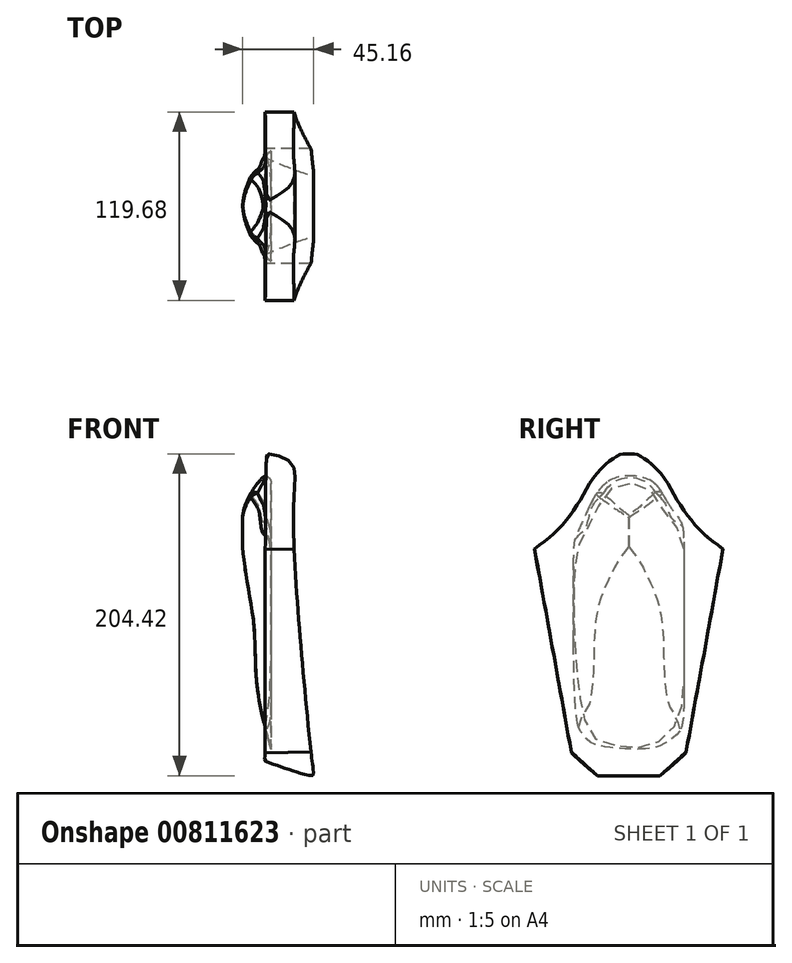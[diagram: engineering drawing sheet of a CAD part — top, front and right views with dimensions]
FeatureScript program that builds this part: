
annotation { "Feature Type Name" : "Feature", "Feature Type Description" : "" }
export const myFeature = defineFeature(function(context is Context, id is Id, definition is map)
    precondition{}
    {
        {
            var Q0;
            Q0=qCreatedBy(makeId("Right.planeOp"),FACE);
            var sketch = newSketch(context, id + "F0", { "sketchPlane" : qUnion([Q0])});
            skFitSpline(sketch, "E0", {"points": [v(0, 116.17) * mm, v(3.06, 115.78) * mm, v(7.67, 113.9) * mm, v(14.22, 108.94) * mm, v(22.25, 100.28) * mm, v(32.3, 83.46) * mm, v(42.34, 70.02) * mm, v(50.07, 62.3) * mm, v(59.84, 54.97) * mm], "startDerivative": vector(42.97, -3.15) * mm, "endDerivative": vector(75.08, -53.22) * mm});
            skLineSegment(sketch, "E1", {"start": v(59.84, 54.97) * mm, "end": v(36.42, -74.25) * mm});
            skLineSegment(sketch, "E2", {"start": v(36.42, -74.25) * mm, "end": v(17.78, -91.38) * mm});
            skLineSegment(sketch, "E3", {"start": v(17.78, -91.38) * mm, "end": v(0, -91.38) * mm});
            skLineSegment(sketch, "E4.MirrorCS", {"start": v(-59.84, 54.97) * mm, "end": v(-36.42, -74.25) * mm});
            skLineSegment(sketch, "E5.MirrorCS", {"start": v(-36.42, -74.25) * mm, "end": v(-17.78, -91.38) * mm});
            skLineSegment(sketch, "E6.MirrorCS", {"start": v(-17.78, -91.38) * mm, "end": v(0, -91.38) * mm});
            skFitSpline(sketch, "E7.MirrorCS", {"points": [v(0, 116.17) * mm, v(-3.06, 115.78) * mm, v(-7.67, 113.9) * mm, v(-14.22, 108.94) * mm, v(-22.25, 100.28) * mm, v(-32.3, 83.46) * mm, v(-42.34, 70.02) * mm, v(-50.07, 62.3) * mm, v(-59.84, 54.97) * mm], "startDerivative": vector(-42.97, -3.15) * mm, "endDerivative": vector(-75.08, -53.22) * mm});
            skSolve(sketch);
        }
        {
            var Q0;
            Q0=makeQuery(id+"F0.imprint","IMPRINT",FACE,{"disambiguationData":[TD([[makeQuery(id+"F0.imprint","IMPRINT",EDGE,{"derivedFrom":sQuery(id+"F0.wireOp",EDGE,"E0")}),-1.0]])]});
            extrude(context, id + "F1", {"entities" : qUnion([Q0]), "depth" : 100 * mm, "offsetDistance" : 25 * mm});
        }
        {
            var Q0;
            Q0=qCreatedBy(makeId("Front.planeOp"),FACE);
            cPlane(context, id + "F2", {"entities" : qUnion([Q0]), "cplaneType" : CPlaneType.OFFSET, "offset" : 75 * mm, "width" : 150 * mm, "height" : 150 * mm});
        }
        {
            var Q0;
            Q0=qCreatedBy(id+"F2.planeOp",FACE);
            var sketch = newSketch(context, id + "F3", { "sketchPlane" : qUnion([Q0])});
            skFitSpline(sketch, "E8", {"points": [v(31.56, 115.61) * mm, v(44.65, 110.3) * mm, v(46.26, 81.32) * mm, v(54.88, -85.85) * mm, v(53.7, -89.38) * mm, v(25.68, -79.97) * mm, v(24.31, -77.23) * mm, v(29.8, 112.28) * mm, v(31.56, 115.61) * mm]});
            skSolve(sketch);
        }
        {
            var Q0;
            Q0=makeQuery(id+"F3.imprint","IMPRINT",FACE,{"disambiguationData":[TD([[makeQuery(id+"F3.imprint","IMPRINT",EDGE,{"derivedFrom":sQuery(id+"F3.wireOp",EDGE,"E8")}),-1.0]])]});
            extrude(context, id + "F4", {"entities" : qUnion([Q0]), "oppositeDirection" : true, "depth" : 146 * mm, "offsetDistance" : 25 * mm});
        }
        {
            var Q0;
            Q0=makeQuery(id+"F1.opExtrude","SWEPT_BODY",BODY,{"disambiguationData":[OSD([sQuery(id+"F0.wireOp",EDGE,"E0"),sQuery(id+"F0.wireOp",EDGE,"E1"),sQuery(id+"F0.wireOp",EDGE,"E2"),sQuery(id+"F0.wireOp",EDGE,"E3"),sQuery(id+"F0.wireOp",EDGE,"E4.MirrorCS"),sQuery(id+"F0.wireOp",EDGE,"E5.MirrorCS"),sQuery(id+"F0.wireOp",EDGE,"E6.MirrorCS"),sQuery(id+"F0.wireOp",EDGE,"E7.MirrorCS")])]});
            var Q1;
            Q1=makeQuery(id+"F4.opExtrude","SWEPT_BODY",BODY,{"disambiguationData":[OSD([sQuery(id+"F3.wireOp",EDGE,"E8")])]});
            booleanBodies(context, id + "F5", {"operationType" : BooleanOperationType.INTERSECTION, "tools" : qUnion([Q0, Q1])});
        }
        {
            var Q0;
            Q0=qCreatedBy(makeId("Top.planeOp"),FACE);
            cPlane(context, id + "F6", {"entities" : qUnion([Q0]), "cplaneType" : CPlaneType.OFFSET, "offset" : 90 * mm, "oppositeDirection" : true, "width" : 150 * mm, "height" : 150 * mm});
        }
        {
            var Q0;
            Q0=qCreatedBy(id+"F6.planeOp",FACE);
            var sketch = newSketch(context, id + "F7", { "sketchPlane" : qUnion([Q0])});
            skLineSegment(sketch, "E9", {"start": v(24.4, -31.72) * mm, "end": v(24.4, 31.99) * mm});
            skFitSpline(sketch, "E10", {"points": [v(24.4, -31.72) * mm, v(24, -30.15) * mm, v(23.4, -28.17) * mm, v(22.63, -25.84) * mm, v(21.8, -23.1) * mm, v(20.57, -19.74) * mm, v(19.28, -18.14) * mm, v(17.6, -15.89) * mm, v(16, -11.54) * mm, v(15.35, -7.88) * mm, v(15.2, -4.37) * mm, v(15.16, -0.02) * mm], "startDerivative": vector(-5.56, 22.83) * mm, "endDerivative": vector(-0.25, 40.72) * mm});
            skFitSpline(sketch, "E11.MirrorCS", {"points": [v(24.4, 31.72) * mm, v(24, 30.15) * mm, v(23.4, 28.17) * mm, v(22.63, 25.84) * mm, v(21.8, 23.1) * mm, v(20.57, 19.74) * mm, v(19.28, 18.14) * mm, v(17.6, 15.89) * mm, v(16, 11.54) * mm, v(15.35, 7.88) * mm, v(15.2, 4.37) * mm, v(15.16, 0.02) * mm], "startDerivative": vector(-5.56, -22.83) * mm, "endDerivative": vector(-0.25, -40.72) * mm});
            skFitSpline(sketch, "E12", {"points": [v(15.16, -0.02) * mm, v(15.16, 0.02) * mm], "startDerivative": vector(0, 0.04) * mm, "endDerivative": vector(0, 0.04) * mm});
            skSolve(sketch);
        }
        {
            var Q0;
            Q0=makeQuery(id+"F5.opBoolean","INTERSECT",BODY,{"derivedFrom":[makeQuery(id+"F1.opExtrude","SWEPT_BODY",BODY,{"disambiguationData":[OSD([sQuery(id+"F0.wireOp",EDGE,"E0"),sQuery(id+"F0.wireOp",EDGE,"E1"),sQuery(id+"F0.wireOp",EDGE,"E2"),sQuery(id+"F0.wireOp",EDGE,"E3"),sQuery(id+"F0.wireOp",EDGE,"E4.MirrorCS"),sQuery(id+"F0.wireOp",EDGE,"E5.MirrorCS"),sQuery(id+"F0.wireOp",EDGE,"E6.MirrorCS"),sQuery(id+"F0.wireOp",EDGE,"E7.MirrorCS")])]}),makeQuery(id+"F4.opExtrude","SWEPT_BODY",BODY,{"disambiguationData":[OSD([sQuery(id+"F3.wireOp",EDGE,"E8")])]})]});
            transform(context, id + "F8", {"entities" : qUnion([Q0]), "transformType" : TransformType.TRANSLATION_3D, "dx" : -23.7 * mm, "dy" : 0 * mm, "dz" : 0 * mm, "makeCopy" : false});
        }
        {
            var Q0;
            {var subQ0=sQuery(id+"F7.wireOp",EDGE,"E10");Q0=makeQuery(id+"F7.imprint","IMPRINT",FACE,{"disambiguationData":[TD([[makeQuery(id+"F7.imprint","IMPRINT",EDGE,{"derivedFrom":subQ0}),-1.0]])]});}
            extrude(context, id + "F9", {"entities" : qUnion([Q0]), "oppositeDirection" : true, "depth" : 25 * mm, "offsetDistance" : 25 * mm});
        }
        {
            var Q0;
            Q0=makeQuery(id+"F5.opBoolean","INTERSECT",BODY,{"derivedFrom":[makeQuery(id+"F1.opExtrude","SWEPT_BODY",BODY,{"disambiguationData":[OSD([sQuery(id+"F0.wireOp",EDGE,"E0"),sQuery(id+"F0.wireOp",EDGE,"E1"),sQuery(id+"F0.wireOp",EDGE,"E2"),sQuery(id+"F0.wireOp",EDGE,"E3"),sQuery(id+"F0.wireOp",EDGE,"E4.MirrorCS"),sQuery(id+"F0.wireOp",EDGE,"E5.MirrorCS"),sQuery(id+"F0.wireOp",EDGE,"E6.MirrorCS"),sQuery(id+"F0.wireOp",EDGE,"E7.MirrorCS")])]}),makeQuery(id+"F4.opExtrude","SWEPT_BODY",BODY,{"disambiguationData":[OSD([sQuery(id+"F3.wireOp",EDGE,"E8")])]})]});
            var Q1;
            Q1=makeQuery(id+"F9.opExtrude","CAP_EDGE",EDGE,{"disambiguationData":[OSD([sQuery(id+"F7.wireOp",EDGE,"E9")])],"isStart":true});
            transform(context, id + "F10", {"entities" : qUnion([Q0]), "transformType" : TransformType.ROTATION, "transformAxis" : qUnion([Q1]), "angle" : 1.35 * degree, "oppositeDirection" : true, "makeCopy" : false});
        }
        {
            var Q0;
            Q0=makeQuery(id+"F9.opExtrude","SWEPT_BODY",BODY,{"disambiguationData":[OSD([sQuery(id+"F7.wireOp",EDGE,"E9"),sQuery(id+"F7.wireOp",EDGE,"E10"),sQuery(id+"F7.wireOp",EDGE,"E11.MirrorCS"),sQuery(id+"F7.wireOp",EDGE,"E12")])]});
            deleteBodies(context, id + "F11", {"entities" : qUnion([Q0])});
        }
        {
            var Q0;
            Q0=qCreatedBy(makeId("Front.planeOp"),FACE);
            var sketch = newSketch(context, id + "F12", { "sketchPlane" : qUnion([Q0])});
            skLineSegment(sketch, "E13", {"start": v(-30.4, 103.45) * mm, "end": v(-30.4, -72.87) * mm});
            skFitSpline(sketch, "E14", {"points": [v(-30.4, 103.45) * mm, v(-35.45, 100.36) * mm, v(-43.9, 89.17) * mm, v(-48.84, 73.76) * mm, v(-47.56, 46.6) * mm, v(-43.7, 22.57) * mm, v(-40.96, 0.92) * mm, v(-39.3, -33.03) * mm, v(-30.4, -72.87) * mm], "startDerivative": vector(-74.42, -34.6) * mm, "endDerivative": vector(64.25, -232.85) * mm});
            skSolve(sketch);
        }
        {
            var Q0;
            Q0=makeQuery(id+"F12.imprint","IMPRINT",FACE,{"disambiguationData":[TD([[makeQuery(id+"F12.imprint","IMPRINT",EDGE,{"derivedFrom":sQuery(id+"F12.wireOp",EDGE,"E13")}),-1.0]])]});
            extrude(context, id + "F13", {"entities" : qUnion([Q0]), "endBound" : BoundingType.SYMMETRIC, "depth" : 70 * mm, "offsetDistance" : 25 * mm});
        }
        {
            var Q0;
            Q0=qCreatedBy(id+"F6.planeOp",FACE);
            var sketch = newSketch(context, id + "F14", { "sketchPlane" : qUnion([Q0])});
            skFitSpline(sketch, "E15", {"points": [v(-29.59, -35.48) * mm, v(-31.45, -34.37) * mm, v(-35.74, -30.03) * mm, v(-37.5, -25.37) * mm, v(-40.16, -22.47) * mm, v(-43.6, -18.28) * mm, v(-46.11, -12.1) * mm, v(-47.49, -7.52) * mm, v(-48.63, -0.12) * mm], "startDerivative": vector(-19.9, 10.35) * mm, "endDerivative": vector(-6.7, 52.44) * mm});
            skFitSpline(sketch, "E16.MirrorCS", {"points": [v(-29.59, 35.48) * mm, v(-31.45, 34.37) * mm, v(-35.74, 30.03) * mm, v(-37.5, 25.37) * mm, v(-40.16, 22.47) * mm, v(-43.6, 18.28) * mm, v(-46.11, 12.1) * mm, v(-47.49, 7.52) * mm, v(-48.63, 0.12) * mm], "startDerivative": vector(-19.9, -10.35) * mm, "endDerivative": vector(-6.7, -52.44) * mm});
            skFitSpline(sketch, "E17", {"points": [v(-48.63, -0.12) * mm, v(-48.63, 0.12) * mm], "startDerivative": vector(0, 0.24) * mm, "endDerivative": vector(0, 0.24) * mm});
            skFitSpline(sketch, "E18", {"points": [v(-29.59, -35.48) * mm, v(-33.07, -37.37) * mm, v(-41.1, -38.88) * mm, v(-50.76, -37.59) * mm, v(-55.94, -17.68) * mm, v(-56.15, 12.74) * mm, v(-57.23, 36.15) * mm, v(-50.92, 40.3) * mm, v(-41.7, 39.77) * mm, v(-30.96, 36.53) * mm, v(-29.59, 35.48) * mm], "startDerivative": vector(-51.56, -34.67) * mm, "endDerivative": vector(23.33, -25.13) * mm});
            skSolve(sketch);
        }
        {
            var Q0;
            Q0=makeQuery(id+"F14.imprint","IMPRINT",FACE,{"disambiguationData":[TD([[makeQuery(id+"F14.imprint","IMPRINT",EDGE,{"derivedFrom":sQuery(id+"F14.wireOp",EDGE,"E15")}),1.0]])]});
            extrude(context, id + "F15", {"entities" : qUnion([Q0]), "operationType" : NewBodyOperationType.REMOVE, "depth" : 196.6 * mm, "offsetDistance" : 25 * mm});
        }
        {
            var Q0;
            Q0=qCreatedBy(makeId("Right.planeOp"),FACE);
            cPlane(context, id + "F16", {"entities" : qUnion([Q0]), "cplaneType" : CPlaneType.OFFSET, "offset" : 55.8 * mm, "oppositeDirection" : true, "width" : 150 * mm, "height" : 150 * mm});
        }
        {
            var Q0;
            Q0=qCreatedBy(id+"F16.planeOp",FACE);
            var sketch = newSketch(context, id + "F17", { "sketchPlane" : qUnion([Q0])});
            skFitSpline(sketch, "E19", {"points": [v(38.7, 61.75) * mm, v(28.45, 78.99) * mm, v(20.37, 91.64) * mm, v(14.45, 97.92) * mm, v(2.05, 101.46) * mm, v(-11.23, 98.68) * mm, v(-21.52, 88.15) * mm, v(-32.87, 65.68) * mm, v(-38.32, 51.93) * mm, v(-33.3, -53.67) * mm, v(-21.08, -71.78) * mm, v(-7.56, -75.06) * mm, v(5.1, -76.37) * mm, v(21.25, -72.22) * mm, v(35, -57.6) * mm, v(39.57, -36.87) * mm, v(38.7, 61.75) * mm]});
            skCircle(sketch, "E20", {"center": v(2.4, 18.7) * mm, "radius": 126.46 * mm});
            skSolve(sketch);
        }
        {
            var Q0;
            Q0=makeQuery(id+"F17.imprint","IMPRINT",FACE,{"disambiguationData":[TD([[makeQuery(id+"F17.imprint","IMPRINT",EDGE,{"derivedFrom":sQuery(id+"F17.wireOp",EDGE,"E19")}),-1.0]])]});
            extrude(context, id + "F18", {"entities" : qUnion([Q0]), "operationType" : NewBodyOperationType.REMOVE, "depth" : 46 * mm, "offsetDistance" : 25 * mm});
        }
        {
            var Q0;
            Q0=makeQuery(id+"F13.opExtrude","SWEPT_BODY",BODY,{"disambiguationData":[OSD([sQuery(id+"F12.wireOp",EDGE,"E13"),sQuery(id+"F12.wireOp",EDGE,"E14")])]});
            transform(context, id + "F19", {"entities" : qUnion([Q0]), "transformType" : TransformType.TRANSLATION_3D, "dx" : 34.8 * mm, "dy" : 0 * mm, "dz" : 0 * mm, "makeCopy" : false});
        }
        {
            var Q0;
            Q0=makeQuery(id+"F15.boolean.opBoolean","SPLIT",FACE,{"disambiguationData":[OD(0.0)],"derivedFrom":makeQuery(id+"F13.opExtrude","SWEPT_FACE",FACE,{"disambiguationData":[OSD([sQuery(id+"F12.wireOp",EDGE,"E14")])]})});
            var Q1;
            {var subQ0=sQuery(id+"F12.wireOp",EDGE,"E14");var subQ1=sQuery(id+"F12.wireOp",EDGE,"E13");Q1=makeQuery(id+"F18.boolean.opBoolean","COPY",FACE,{"disambiguationData":[TD([makeQuery(id+"F13.opExtrude","SWEPT_FACE",FACE,{"disambiguationData":[OSD([subQ1])]}),makeQuery(id+"F13.opExtrude","CAP_FACE",FACE,{"disambiguationData":[OSD([subQ1,subQ0])],"isStart":true}),makeQuery(id+"F13.opExtrude","CAP_FACE",FACE,{"disambiguationData":[OSD([subQ1,subQ0])],"isStart":false}),makeQuery(id+"F13.opExtrude","SWEPT_FACE",FACE,{"disambiguationData":[OSD([subQ0])]}),makeQuery(id+"F15.boolean.opBoolean","COPY",FACE,{"derivedFrom":makeQuery(id+"F15.opExtrude","SWEPT_FACE",FACE,{"disambiguationData":[OSD([sQuery(id+"F14.wireOp",EDGE,"E15")])]})}),makeQuery(id+"F15.boolean.opBoolean","COPY",FACE,{"derivedFrom":makeQuery(id+"F15.opExtrude","SWEPT_FACE",FACE,{"disambiguationData":[OSD([sQuery(id+"F14.wireOp",EDGE,"E16.MirrorCS")])]})})])],"derivedFrom":makeQuery(id+"F18.opExtrude","SWEPT_FACE",FACE,{"disambiguationData":[OSD([sQuery(id+"F17.wireOp",EDGE,"E19")])]})});}
            fillet(context, id + "F20", {"entities" : qUnion([Q0, Q1]), "radius" : 5 * mm, "tangentPropagation" : true, "allowEdgeOverflow" : false});
        }
    });
